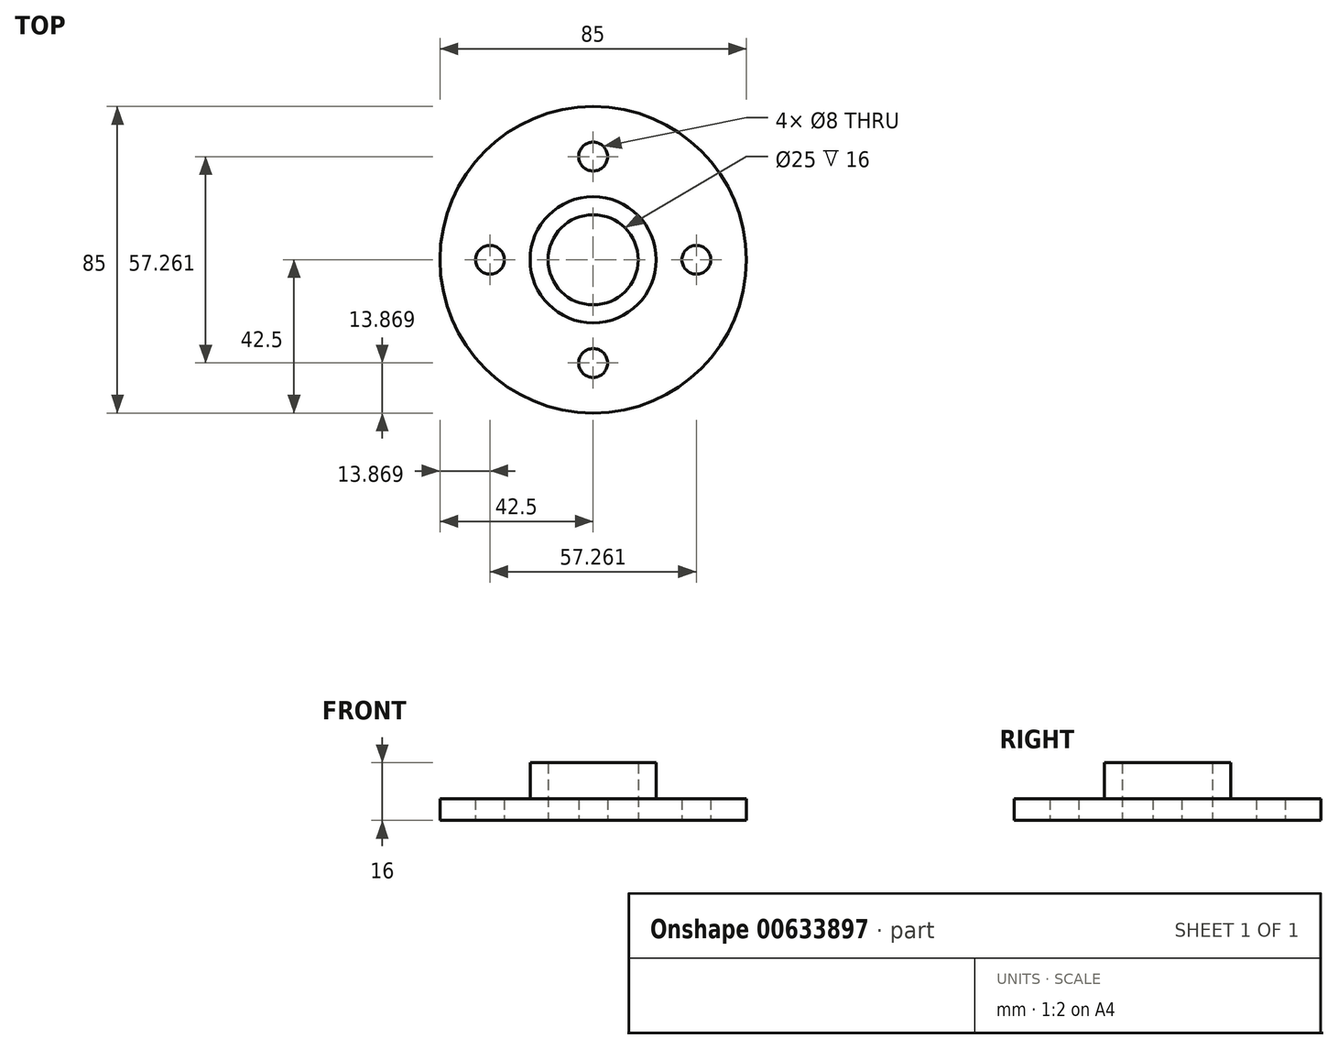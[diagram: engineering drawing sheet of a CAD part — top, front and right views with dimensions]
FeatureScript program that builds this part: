
annotation { "Feature Type Name" : "Feature", "Feature Type Description" : "" }
export const myFeature = defineFeature(function(context is Context, id is Id, definition is map)
    precondition{}
    {
        {
            var Q0;
            Q0=qCreatedBy(makeId("Top.planeOp"),FACE);
            var sketch = newSketch(context, id + "F0", { "sketchPlane" : qUnion([Q0])});
            skCircle(sketch, "E0", {"center": v(0, 0) * mm, "radius": 42.5 * mm});
            skCircle(sketch, "E1", {"center": v(0, 0) * mm, "radius": 12.5 * mm});
            skCircle(sketch, "E2", {"center": v(-28.63, 0) * mm, "radius": 4 * mm});
            skCircle(sketch, "E3", {"center": v(0, 0) * mm, "radius": 28.63 * mm, "construction": true});
            skCircle(sketch, "E4.1.0", {"center": v(0, -28.63) * mm, "radius": 4 * mm});
            skCircle(sketch, "E4.2.0", {"center": v(28.63, 0) * mm, "radius": 4 * mm});
            skCircle(sketch, "E4.3.0", {"center": v(0, 28.63) * mm, "radius": 4 * mm});
            skSolve(sketch);
        }
        {
            var Q0;
            Q0=makeQuery(id+"F0.imprint","IMPRINT",FACE,{"disambiguationData":[TD([[makeQuery(id+"F0.imprint","IMPRINT",EDGE,{"derivedFrom":sQuery(id+"F0.wireOp",EDGE,"E0")}),1.0]])]});
            extrude(context, id + "F1", {"entities" : qUnion([Q0]), "depth" : 6 * mm, "offsetDistance" : 25 * mm});
        }
        {
            var Q0;
            Q0=makeQuery(id+"F1.opExtrude","CAP_FACE",FACE,{"disambiguationData":[OSD([sQuery(id+"F0.wireOp",EDGE,"E0"),sQuery(id+"F0.wireOp",EDGE,"E1"),sQuery(id+"F0.wireOp",EDGE,"E2"),sQuery(id+"F0.wireOp",EDGE,"E4.1.0"),sQuery(id+"F0.wireOp",EDGE,"E4.2.0"),sQuery(id+"F0.wireOp",EDGE,"E4.3.0")])],"isStart":false});
            var sketch = newSketch(context, id + "F2", { "sketchPlane" : qUnion([Q0])});
            skCircle(sketch, "E5.0", {"center": v(0, 0) * mm, "radius": 12.5 * mm});
            skCircle(sketch, "E6", {"center": v(0, 0) * mm, "radius": 17.5 * mm});
            skSolve(sketch);
        }
        {
            var Q0;
            Q0 = qSketchRegion(id + "F2", true);
            extrude(context, id + "F3", {"entities" : qUnion([Q0]), "operationType" : NewBodyOperationType.ADD, "depth" : 10 * mm, "offsetDistance" : 25 * mm});
        }
    });
